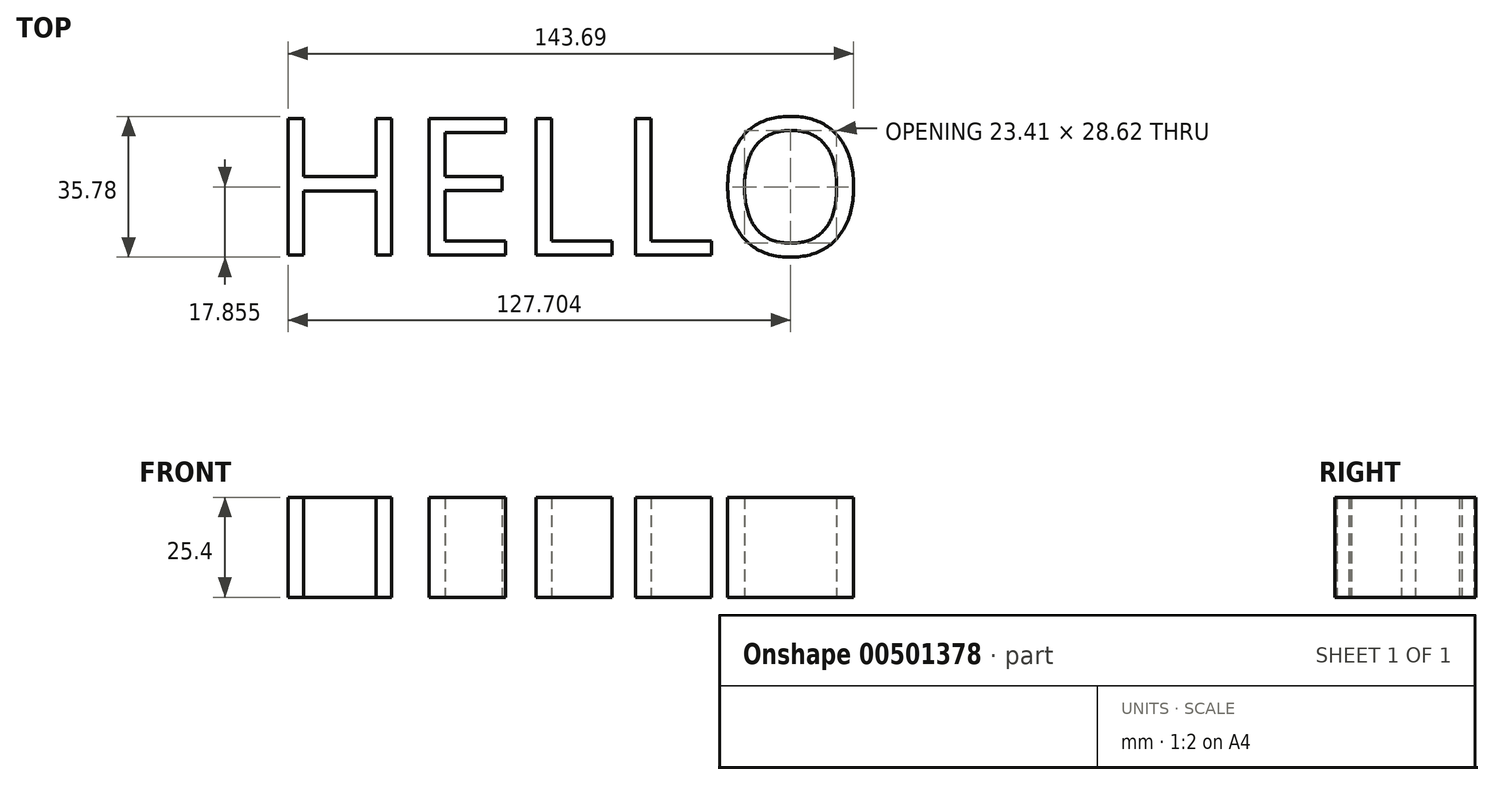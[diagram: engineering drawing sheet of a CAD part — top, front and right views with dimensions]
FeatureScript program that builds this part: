
annotation { "Feature Type Name" : "Feature", "Feature Type Description" : "" }
export const myFeature = defineFeature(function(context is Context, id is Id, definition is map)
    precondition{}
    {
        {
            var Q0;
            Q0=qCreatedBy(makeId("Top.planeOp"),FACE);
            var sketch = newSketch(context, id + "F0", { "sketchPlane" : qUnion([Q0])});
            skText(sketch, "E0", { "text": "HELLO", "fontName": "OpenSans-Regular.ttf"});
            const initialGuessF0  = {"E0": [-0.06164, 0.022, 1, 0, 0.03505]};
            skSetInitialGuess(sketch, initialGuessF0);
            skSolve(sketch);
        }
        {
            var Q0;
            Q0 = qSketchRegion(id + "F0", true);
            extrude(context, id + "F1", {"entities" : qUnion([Q0]), "depth" : 25.4 * mm});
        }
        {
            var Q0;
            Q0=makeQuery(id+"F1.opExtrude","SWEPT_BODY",BODY,{"disambiguationData":[OSD([sQuery(id+"F0.wireOp",EDGE,"E0.sketch_text.stroke-0"),sQuery(id+"F0.wireOp",EDGE,"E0.sketch_text.stroke-1"),sQuery(id+"F0.wireOp",EDGE,"E0.sketch_text.stroke-2"),sQuery(id+"F0.wireOp",EDGE,"E0.sketch_text.stroke-3"),sQuery(id+"F0.wireOp",EDGE,"E0.sketch_text.stroke-4"),sQuery(id+"F0.wireOp",EDGE,"E0.sketch_text.stroke-5"),sQuery(id+"F0.wireOp",EDGE,"E0.sketch_text.stroke-6"),sQuery(id+"F0.wireOp",EDGE,"E0.sketch_text.stroke-7"),sQuery(id+"F0.wireOp",EDGE,"E0.sketch_text.stroke-8"),sQuery(id+"F0.wireOp",EDGE,"E0.sketch_text.stroke-9"),sQuery(id+"F0.wireOp",EDGE,"E0.sketch_text.stroke-10"),sQuery(id+"F0.wireOp",EDGE,"E0.sketch_text.stroke-11")])]});
            var Q1;
            Q1=makeQuery(id+"F1.opExtrude","SWEPT_BODY",BODY,{"disambiguationData":[OSD([sQuery(id+"F0.wireOp",EDGE,"E0.sketch_text.stroke-12"),sQuery(id+"F0.wireOp",EDGE,"E0.sketch_text.stroke-13"),sQuery(id+"F0.wireOp",EDGE,"E0.sketch_text.stroke-14"),sQuery(id+"F0.wireOp",EDGE,"E0.sketch_text.stroke-15"),sQuery(id+"F0.wireOp",EDGE,"E0.sketch_text.stroke-16"),sQuery(id+"F0.wireOp",EDGE,"E0.sketch_text.stroke-17"),sQuery(id+"F0.wireOp",EDGE,"E0.sketch_text.stroke-18"),sQuery(id+"F0.wireOp",EDGE,"E0.sketch_text.stroke-19"),sQuery(id+"F0.wireOp",EDGE,"E0.sketch_text.stroke-20"),sQuery(id+"F0.wireOp",EDGE,"E0.sketch_text.stroke-21"),sQuery(id+"F0.wireOp",EDGE,"E0.sketch_text.stroke-22"),sQuery(id+"F0.wireOp",EDGE,"E0.sketch_text.stroke-23")])]});
            var Q2;
            Q2=makeQuery(id+"F1.opExtrude","SWEPT_BODY",BODY,{"disambiguationData":[OSD([sQuery(id+"F0.wireOp",EDGE,"E0.sketch_text.stroke-24"),sQuery(id+"F0.wireOp",EDGE,"E0.sketch_text.stroke-25"),sQuery(id+"F0.wireOp",EDGE,"E0.sketch_text.stroke-26"),sQuery(id+"F0.wireOp",EDGE,"E0.sketch_text.stroke-27"),sQuery(id+"F0.wireOp",EDGE,"E0.sketch_text.stroke-28"),sQuery(id+"F0.wireOp",EDGE,"E0.sketch_text.stroke-29")])]});
            var Q3;
            Q3=makeQuery(id+"F1.opExtrude","SWEPT_BODY",BODY,{"disambiguationData":[OSD([sQuery(id+"F0.wireOp",EDGE,"E0.sketch_text.stroke-30"),sQuery(id+"F0.wireOp",EDGE,"E0.sketch_text.stroke-31"),sQuery(id+"F0.wireOp",EDGE,"E0.sketch_text.stroke-32"),sQuery(id+"F0.wireOp",EDGE,"E0.sketch_text.stroke-33"),sQuery(id+"F0.wireOp",EDGE,"E0.sketch_text.stroke-34"),sQuery(id+"F0.wireOp",EDGE,"E0.sketch_text.stroke-35")])]});
            var Q4;
            Q4=makeQuery(id+"F1.opExtrude","SWEPT_BODY",BODY,{"disambiguationData":[OSD([sQuery(id+"F0.wireOp",EDGE,"E0.sketch_text.stroke-36"),sQuery(id+"F0.wireOp",EDGE,"E0.sketch_text.stroke-37"),sQuery(id+"F0.wireOp",EDGE,"E0.sketch_text.stroke-38"),sQuery(id+"F0.wireOp",EDGE,"E0.sketch_text.stroke-39"),sQuery(id+"F0.wireOp",EDGE,"E0.sketch_text.stroke-40"),sQuery(id+"F0.wireOp",EDGE,"E0.sketch_text.stroke-41"),sQuery(id+"F0.wireOp",EDGE,"E0.sketch_text.stroke-42"),sQuery(id+"F0.wireOp",EDGE,"E0.sketch_text.stroke-43"),sQuery(id+"F0.wireOp",EDGE,"E0.sketch_text.stroke-44"),sQuery(id+"F0.wireOp",EDGE,"E0.sketch_text.stroke-45"),sQuery(id+"F0.wireOp",EDGE,"E0.sketch_text.stroke-46"),sQuery(id+"F0.wireOp",EDGE,"E0.sketch_text.stroke-47"),sQuery(id+"F0.wireOp",EDGE,"E0.sketch_text.stroke-48"),sQuery(id+"F0.wireOp",EDGE,"E0.sketch_text.stroke-49"),sQuery(id+"F0.wireOp",EDGE,"E0.sketch_text.stroke-50"),sQuery(id+"F0.wireOp",EDGE,"E0.sketch_text.stroke-51")])]});
            transform(context, id + "F2", {"entities" : qUnion([Q0, Q1, Q2, Q3, Q4]), "transformType" : TransformType.TRANSLATION_3D, "dx" : -13.72 * mm, "dy" : -2.03 * mm, "dz" : 0 * mm, "makeCopy" : false});
        }
    });
